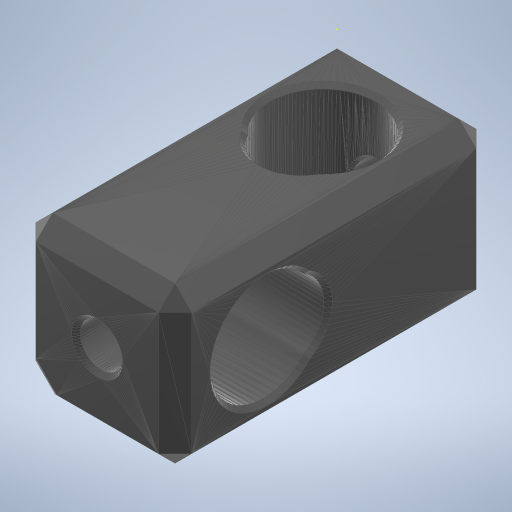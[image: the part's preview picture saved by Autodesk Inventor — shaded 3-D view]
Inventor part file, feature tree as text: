
AUTODESK INVENTOR PART (.ipt)
format: ipt  version: 2023 (Build 270158000, 158)  size: 305,152 bytes
history: native  units: in
note: dims shown in document units (in); Inventor stores cm internally (conversion verified against a paired STEP export)
features: other x2, sketch x1
ambient origin geometry x8: Origin, YZ Plane, XZ Plane, XY Plane, X Axis, Y Axis, Z Axis, Center Point
feature tree (3):
  other  "ra90k"
  sketch  "Sketch3"
  other  "MeshFeature1"
